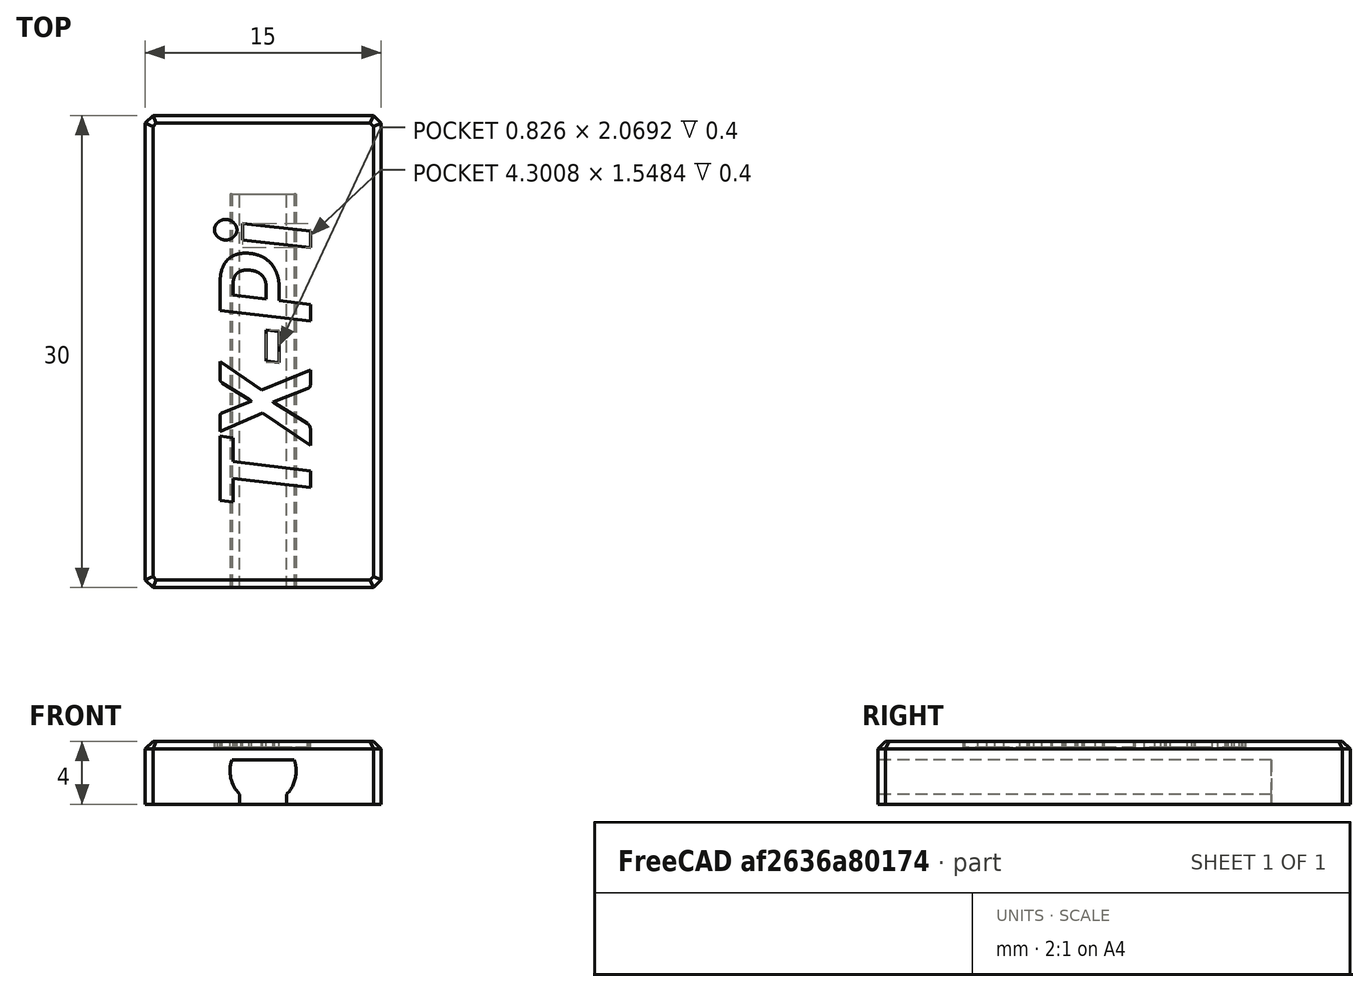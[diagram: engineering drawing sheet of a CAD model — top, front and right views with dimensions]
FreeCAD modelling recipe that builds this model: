
FCSTD DOCUMENT  (FreeCAD 0.17RUnknown)
Label: Abdeckplatte_TX-Pi-15x30x4
License: All rights reserved
LicenseURL: http://en.wikipedia.org/wiki/All_rights_reserved
objects: Part::Box×3, Part::Cut×3, Part::Chamfer×2, Part::Cylinder×1, Part::MultiFuse×1, Part::Part2DObjectPython×1, Part::Extrusion×1
note: 12 computed .brp shape members not serialized (recipe doc carries the construction recipe); baked Part::Feature solids carry a one-line shape summary decoded from their .brp

FEATURE [Part::Box] Box  label="Basis 15x30x5"
  AttacherType = Attacher::AttachEngine3D
  Height = 4
  Length = 15
  Width = 30
FEATURE [Part::Box] Box001  label="Nut 3x25x2"
  AttacherType = Attacher::AttachEngine3D
  Height = 2
  Length = 3
  Placement = pos=(6,0,0) rot=(0,0,1;0rad)
  Width = 25
FEATURE [Part::Cylinder] Cylinder  label="bohrung"
  Angle = 360
  AttacherType = Attacher::AttachEngine3D
  Height = 25
  Placement = pos=(0,0,0) rot=(1,0,0;1.5708rad)
  Radius = 2.1
FEATURE [Part::Box] Box002  label="Abflachung"
  AttacherType = Attacher::AttachEngine3D
  Height = 2
  Length = 4
  Placement = pos=(-2,-25,0.7) rot=(0,0,1;0rad)
  Width = 25
FEATURE [Part::Cut] Cut  label="Kreisnut 4x25"
  Base = -> Cylinder
  Placement = pos=(7.5,25,2.1) rot=(0,0,1;0rad)
  Tool = -> Box002
FEATURE [Part::MultiFuse] Fusion
  Shapes = -> [Box001,Cut]
FEATURE [Part::Cut] Cut001
  Base = -> Box
  Tool = -> Fusion
FEATURE [Part::Chamfer] Chamfer
  Base = -> Cut001
  Edges = 4 edges r=0.5: [Edge1,Edge3,Edge13,Edge18]
FEATURE [Part::Chamfer] Chamfer001  label="Fertigteil"
  Base = -> Chamfer
  Edges = 8 edges r=0.5: [Edge1,Edge5,Edge6,Edge7,Edge8,Edge9,Edge10,Edge11]
FEATURE [Part::Part2DObjectPython] ShapeString  # Draft 2D object (typed FeaturePython)
  FontFile = <path>
  Placement = pos=(10.5,5,4) rot=(0,0,1;1.5708rad)
  Size = 7
  String = TX-Pi
  Tracking = 0
FEATURE [Part::Extrusion] Extrude
  Base = -> ShapeString
  Dir = (0,0,1)
  DirMode = 2
  FaceMakerClass = Part::FaceMakerBullseye
  LengthFwd = 0.4
  LengthRev = 0
  Placement = pos=(0,0,-0.4) rot=(0,0,1;0rad)
  Solid = false
  Symmetric = false
FEATURE [Part::Cut] Cut002
  Base = -> Chamfer001
  Tool = -> Extrude
note: 1 file-system path scrubbed to <path> (originals preserved in the JSON sidecar)
